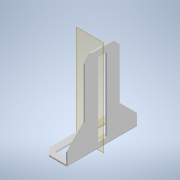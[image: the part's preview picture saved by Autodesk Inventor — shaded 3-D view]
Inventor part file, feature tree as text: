
AUTODESK INVENTOR PART (.ipt)
format: ipt  version: 2020 (Build 240168000, 168)  size: 145,920 bytes
history: native  units: in
note: dims shown in document units (in); Inventor stores cm internally (conversion verified against a paired STEP export)
features: other x2, plane x2, imported_body x1
ambient origin geometry x8: Origin, YZ Plane, XZ Plane, XY Plane, X Axis, Y Axis, Z Axis, Center Point
bodies: Body1 (feature_tree)
feature tree (5):
  other  "Angle Gusset"
  parser-record x1  (decoder bookkeeping rows leaked as tree rows — omitted from the tree; the rows remain in map.json)
  plane  "Work Plane1"
  plane  "Work Plane2"
  imported_body  "Base1"
